# Revit family: 5.Wichmann Kabelbox 3S_DECK
name_source: partatom
category: Mechanical Equipment
revit_build: Autodesk Revit 2018 (Build: 20170223_1515(x64)
units: mm (PartAtom-declared; Revit-internal decimal feet)

## family parameters
Always vertical = Yes
Cut with Voids When Loaded = No
Host = Ceiling
OmniClass Number = 23.75.00.00
OmniClass Title = Climate Control (HVAC)
Part Type = Normal
Room Calculation Point = No
Round Connector Dimension = Use Diameter
Shared = No

## types (50) — shared parameters
Bautiefe = 270 mm
Werkstoff = Stahl

## per-type parameters (varying)
| type | B_i | B_rohbau | Breite | HAN | H_i | H_rohbau | Höhe |
| Kabelbox 3S, 60x120x270 mm | 90 mm  [stored 0.295276 ft] | 160 mm | 120 mm | 3S060120 | 38 mm  [stored 0.124672 ft] | 80 mm  [stored 0.262467 ft] | 60 mm  [stored 0.19685 ft] |
| Kabelbox 3S, 60x160x270 mm | 130 mm | 200 mm  [stored 0.656168 ft] | 160 mm | 3S060160 | 38 mm  [stored 0.124672 ft] | 80 mm  [stored 0.262467 ft] | 60 mm  [stored 0.19685 ft] |
| Kabelbox 3S, 60x200x270 mm | 170 mm | 240 mm | 200 mm  [stored 0.656168 ft] | 3S060200 | 38 mm  [stored 0.124672 ft] | 80 mm  [stored 0.262467 ft] | 60 mm  [stored 0.19685 ft] |
| Kabelbox 3S, 60x240x270 mm | 210 mm | 280 mm | 240 mm | 3S060240 | 38 mm  [stored 0.124672 ft] | 80 mm  [stored 0.262467 ft] | 60 mm  [stored 0.19685 ft] |
| Kabelbox 3S, 60x260x270 mm | 230 mm | 300 mm | 260 mm | 3S060260 | 38 mm  [stored 0.124672 ft] | 80 mm  [stored 0.262467 ft] | 60 mm  [stored 0.19685 ft] |
| Kabelbox 3S, 60x335x270 mm | 305 mm | 375 mm | 335 mm | 3S060335 | 38 mm  [stored 0.124672 ft] | 80 mm  [stored 0.262467 ft] | 60 mm  [stored 0.19685 ft] |
| Kabelbox 3S, 60x360x270 mm | 330 mm | 400 mm | 360 mm | 3S060360 | 38 mm  [stored 0.124672 ft] | 80 mm  [stored 0.262467 ft] | 60 mm  [stored 0.19685 ft] |
| Kabelbox 3S, 60x435x270 mm | 405 mm | 475 mm | 435 mm | 3S060435 | 38 mm  [stored 0.124672 ft] | 80 mm  [stored 0.262467 ft] | 60 mm  [stored 0.19685 ft] |
| Kabelbox 3S, 60x460x270 mm | 430 mm | 500 mm  [stored 1.64042 ft] | 460 mm | 3S060460 | 38 mm  [stored 0.124672 ft] | 80 mm  [stored 0.262467 ft] | 60 mm  [stored 0.19685 ft] |
| Kabelbox 3S, 60x535x270 mm | 505 mm | 575 mm | 535 mm | 3S060535 | 38 mm  [stored 0.124672 ft] | 80 mm  [stored 0.262467 ft] | 60 mm  [stored 0.19685 ft] |
| Kabelbox 3S, 80x120x270 mm | 90 mm  [stored 0.295276 ft] | 160 mm | 120 mm | 3S080120 | 52 mm | 100 mm  [stored 0.328084 ft] | 80 mm  [stored 0.262467 ft] |
| Kabelbox 3S, 80x160x270 mm | 130 mm | 200 mm  [stored 0.656168 ft] | 160 mm | 3S080160 | 52 mm | 100 mm  [stored 0.328084 ft] | 80 mm  [stored 0.262467 ft] |
| Kabelbox 3S, 80x200x270 mm | 170 mm | 240 mm | 200 mm  [stored 0.656168 ft] | 3S080200 | 52 mm | 100 mm  [stored 0.328084 ft] | 80 mm  [stored 0.262467 ft] |
| Kabelbox 3S, 80x240x270 mm | 210 mm | 280 mm | 240 mm | 3S080240 | 52 mm | 103 mm | 86 mm |
| Kabelbox 3S, 80x260x270 mm | 230 mm | 300 mm | 260 mm | 3S080260 | 52 mm | 100 mm  [stored 0.328084 ft] | 80 mm  [stored 0.262467 ft] |
| Kabelbox 3S, 80x335x270 mm | 305 mm | 375 mm | 335 mm | 3S080335 | 52 mm | 100 mm  [stored 0.328084 ft] | 80 mm  [stored 0.262467 ft] |
| Kabelbox 3S, 80x360x270 mm | 330 mm | 400 mm | 360 mm | 3S080360 | 52 mm | 100 mm  [stored 0.328084 ft] | 80 mm  [stored 0.262467 ft] |
| Kabelbox 3S, 80x435x270 mm | 405 mm | 475 mm | 435 mm | 3S080435 | 52 mm | 100 mm  [stored 0.328084 ft] | 80 mm  [stored 0.262467 ft] |
| Kabelbox 3S, 80x460x270 mm | 430 mm | 500 mm  [stored 1.64042 ft] | 460 mm | 3S080460 | 52 mm | 100 mm  [stored 0.328084 ft] | 80 mm  [stored 0.262467 ft] |
| Kabelbox 3S, 80x535x270 mm | 505 mm | 575 mm | 535 mm | 3S080535 | 52 mm | 100 mm  [stored 0.328084 ft] | 80 mm  [stored 0.262467 ft] |
| Kabelbox 3S, 90x120x270 mm | 90 mm  [stored 0.295276 ft] | 160 mm | 120 mm | 3S090120 | 58 mm | 110 mm | 90 mm  [stored 0.295276 ft] |
| Kabelbox 3S, 90x160x270 mm | 130 mm | 200 mm  [stored 0.656168 ft] | 160 mm | 3S090160 | 58 mm | 110 mm | 90 mm  [stored 0.295276 ft] |
| Kabelbox 3S, 90x200x270 mm | 170 mm | 240 mm | 200 mm  [stored 0.656168 ft] | 3S090200 | 58 mm | 110 mm | 90 mm  [stored 0.295276 ft] |
| Kabelbox 3S, 90x240x270 mm | 210 mm | 280 mm | 240 mm | 3S090240 | 58 mm | 110 mm | 90 mm  [stored 0.295276 ft] |
| Kabelbox 3S, 90x260x270 mm | 230 mm | 300 mm | 260 mm | 3S090260 | 58 mm | 110 mm | 90 mm  [stored 0.295276 ft] |
| Kabelbox 3S, 90x335x270 mm | 305 mm | 375 mm | 335 mm | 3S090335 | 58 mm | 110 mm | 90 mm  [stored 0.295276 ft] |
| Kabelbox 3S, 90x360x270 mm | 330 mm | 400 mm | 360 mm | 3S090360 | 58 mm | 110 mm | 90 mm  [stored 0.295276 ft] |
| Kabelbox 3S, 90x435x270 mm | 405 mm | 475 mm | 435 mm | 3S090435 | 58 mm | 110 mm | 90 mm  [stored 0.295276 ft] |
| Kabelbox 3S, 90x460x270 mm | 430 mm | 500 mm  [stored 1.64042 ft] | 460 mm | 3S090460 | 58 mm | 110 mm | 90 mm  [stored 0.295276 ft] |
| Kabelbox 3S, 90x535x270 mm | 505 mm | 575 mm | 535 mm | 3S090535 | 58 mm | 110 mm | 90 mm  [stored 0.295276 ft] |
| Kabelbox 3S, 100x120x270 mm | 90 mm  [stored 0.295276 ft] | 160 mm | 120 mm | 3S100120 | 66 mm | 120 mm | 100 mm  [stored 0.328084 ft] |
| Kabelbox 3S, 100x160x270 mm | 130 mm | 200 mm  [stored 0.656168 ft] | 160 mm | 3S100160 | 66 mm | 120 mm | 100 mm  [stored 0.328084 ft] |
| Kabelbox 3S, 100x200x270 mm | 170 mm | 240 mm | 200 mm  [stored 0.656168 ft] | 3S100200 | 66 mm | 120 mm | 100 mm  [stored 0.328084 ft] |
| Kabelbox 3S, 100x240x270 mm | 210 mm | 280 mm | 240 mm | 3S100240 | 66 mm | 120 mm | 100 mm  [stored 0.328084 ft] |
| Kabelbox 3S, 100x260x270 mm | 230 mm | 300 mm | 260 mm | 3S100260 | 66 mm | 120 mm | 100 mm  [stored 0.328084 ft] |
| Kabelbox 3S, 100x335x270 mm | 305 mm | 375 mm | 335 mm | 3S100335 | 66 mm | 120 mm | 100 mm  [stored 0.328084 ft] |
| Kabelbox 3S, 100x360x270 mm | 330 mm | 400 mm | 360 mm | 3S100360 | 66 mm | 120 mm | 100 mm  [stored 0.328084 ft] |
| Kabelbox 3S, 100x435x270 mm | 405 mm | 475 mm | 435 mm | 3S100435 | 66 mm | 120 mm | 100 mm  [stored 0.328084 ft] |
| Kabelbox 3S, 100x460x270 mm | 430 mm | 500 mm  [stored 1.64042 ft] | 460 mm | 3S100460 | 66 mm | 120 mm | 100 mm  [stored 0.328084 ft] |
| Kabelbox 3S, 100x535x270 mm | 505 mm | 575 mm | 535 mm | 3S100535 | 66 mm | 120 mm | 100 mm  [stored 0.328084 ft] |
| Kabelbox 3S, 110x120x270 mm | 90 mm  [stored 0.295276 ft] | 160 mm | 120 mm | 3S110120 | 75 mm | 130 mm | 110 mm |
| Kabelbox 3S, 110x160x270 mm | 130 mm | 200 mm  [stored 0.656168 ft] | 160 mm | 3S110160 | 75 mm | 130 mm | 110 mm |
| Kabelbox 3S, 110x200x270 mm | 170 mm | 240 mm | 200 mm  [stored 0.656168 ft] | 3S110200 | 75 mm | 130 mm | 110 mm |
| Kabelbox 3S, 110x240x270 mm | 210 mm | 280 mm | 240 mm | 3S110240 | 75 mm | 130 mm | 110 mm |
| Kabelbox 3S, 110x260x270 mm | 230 mm | 300 mm | 260 mm | 3S110260 | 75 mm | 130 mm | 110 mm |
| Kabelbox 3S, 110x335x270 mm | 305 mm | 375 mm | 335 mm | 3S110335 | 75 mm | 130 mm | 110 mm |
| Kabelbox 3S, 110x360x270 mm | 330 mm | 400 mm | 360 mm | 3S110360 | 75 mm | 130 mm | 110 mm |
| Kabelbox 3S, 110x435x270 mm | 405 mm | 475 mm | 435 mm | 3S110435 | 75 mm | 130 mm | 110 mm |
| Kabelbox 3S, 110x460x270 mm | 430 mm | 500 mm  [stored 1.64042 ft] | 460 mm | 3S110460 | 75 mm | 130 mm | 110 mm |
| Kabelbox 3S, 110x535x270 mm | 505 mm | 575 mm | 535 mm | 3S110535 | 75 mm | 130 mm | 110 mm |

note: [stored X ft] marks values corroborated as IEEE doubles in the binary element streams (Revit-internal decimal feet)

## geometry (parser evidence)
native form markers: Sweep x5
no freeform markers — native parametric forms only
